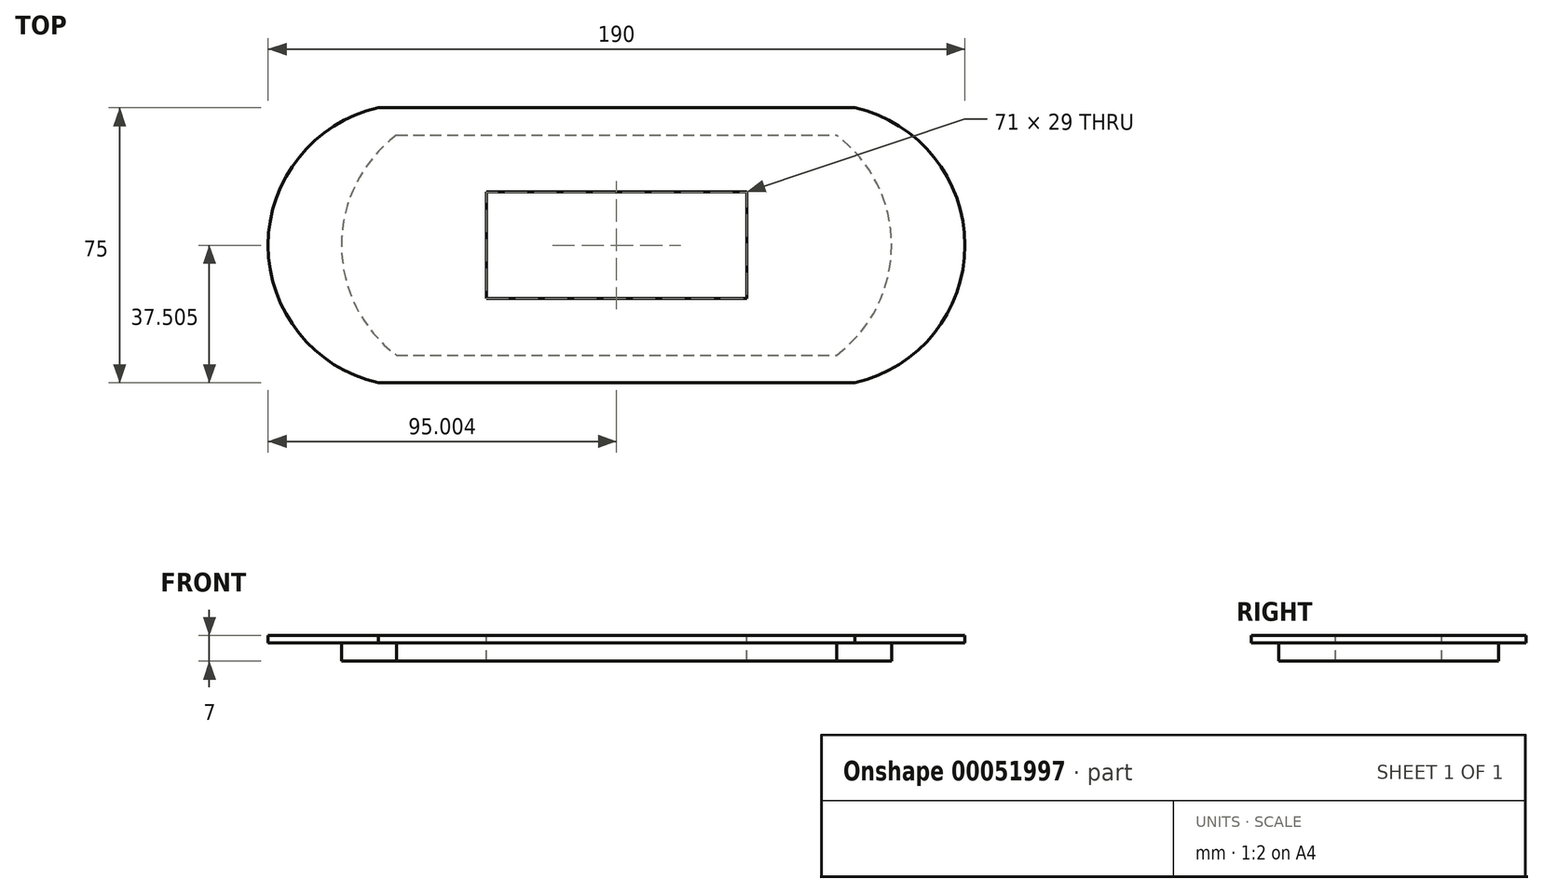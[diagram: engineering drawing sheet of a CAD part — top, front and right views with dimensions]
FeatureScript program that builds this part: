
annotation { "Feature Type Name" : "Feature", "Feature Type Description" : "" }
export const myFeature = defineFeature(function(context is Context, id is Id, definition is map)
    precondition{}
    {
        {
            var Q0;
            Q0=qCreatedBy(makeId("Top.planeOp"),FACE);
            var sketch = newSketch(context, id + "F5", { "sketchPlane" : qUnion([Q0])});
            skLineSegment(sketch, "E0.bottom", {"start": v(43.83, -33.43) * mm, "end": v(233.83, -33.43) * mm, "construction": true});
            skLineSegment(sketch, "E0.top", {"start": v(43.83, 41.57) * mm, "end": v(233.83, 41.57) * mm, "construction": true});
            skLineSegment(sketch, "E0.left", {"start": v(43.83, -33.43) * mm, "end": v(43.83, 41.57) * mm, "construction": true});
            skLineSegment(sketch, "E0.right", {"start": v(233.83, -33.43) * mm, "end": v(233.83, 41.57) * mm, "construction": true});
            skLineSegment(sketch, "E1.bottom", {"start": v(73.83, 41.57) * mm, "end": v(203.83, 41.57) * mm});
            skLineSegment(sketch, "E1.top", {"start": v(73.83, -33.43) * mm, "end": v(203.83, -33.43) * mm});
            skArc(sketch, "E2", {"start": v(73.83, 41.57) * mm, "mid": v(43.83, 4.07) * mm, "end": v(73.83, -33.43) * mm});
            skArc(sketch, "E3", {"start": v(203.83, -33.43) * mm, "mid": v(233.83, 4.07) * mm, "end": v(203.83, 41.57) * mm});
            skSolve(sketch);
        }
        {
            var Q0;
            Q0=makeQuery(id+"F5.imprint","IMPRINT",FACE,{"disambiguationData":[TD([[makeQuery(id+"F5.imprint","IMPRINT",EDGE,{"derivedFrom":sQuery(id+"F5.wireOp",EDGE,"E1.bottom")}),-1.0]])]});
            extrude(context, id + "F0", {"entities" : qUnion([Q0]), "depth" : 2 * mm});
        }
        {
            var Q0;
            Q0=makeQuery(id+"F0.opExtrude","CAP_FACE",FACE,{"disambiguationData":[OSD([sQuery(id+"F5.wireOp",EDGE,"E1.bottom"),sQuery(id+"F5.wireOp",EDGE,"E1.top"),sQuery(id+"F5.wireOp",EDGE,"E2"),sQuery(id+"F5.wireOp",EDGE,"E3")])],"isStart":false});
            var sketch = newSketch(context, id + "F1", { "sketchPlane" : qUnion([Q0])});
            skLineSegment(sketch, "E4.bottom", {"start": v(103.33, 18.57) * mm, "end": v(174.33, 18.57) * mm});
            skLineSegment(sketch, "E4.top", {"start": v(103.33, -10.43) * mm, "end": v(174.33, -10.43) * mm});
            skLineSegment(sketch, "E4.left", {"start": v(103.33, 18.57) * mm, "end": v(103.33, -10.43) * mm});
            skLineSegment(sketch, "E4.right", {"start": v(174.33, 18.57) * mm, "end": v(174.33, -10.43) * mm});
            skLineSegment(sketch, "E5", {"start": v(73.83, 41.57) * mm, "end": v(103.33, 18.57) * mm, "construction": true});
            skLineSegment(sketch, "E6", {"start": v(174.33, -10.43) * mm, "end": v(203.83, -33.43) * mm, "construction": true});
            skLineSegment(sketch, "E7", {"start": v(103.33, -10.43) * mm, "end": v(73.83, -33.43) * mm, "construction": true});
            skLineSegment(sketch, "E8", {"start": v(174.33, 18.57) * mm, "end": v(203.83, 41.57) * mm, "construction": true});
            skSolve(sketch);
        }
        {
            var Q0;
            Q0=makeQuery(id+"F5.imprint","IMPRINT",FACE,{"disambiguationData":[TD([[makeQuery(id+"F5.imprint","IMPRINT",EDGE,{"derivedFrom":sQuery(id+"F5.wireOp",EDGE,"E1.bottom")}),-1.0]])]});
            var sketch = newSketch(context, id + "F2", { "sketchPlane" : qUnion([Q0])});
            skLineSegment(sketch, "E9.bottom", {"start": v(78.83, -25.93) * mm, "end": v(198.83, -25.93) * mm});
            skLineSegment(sketch, "E9.top", {"start": v(78.83, 34.08) * mm, "end": v(198.83, 34.08) * mm});
            skArc(sketch, "E10", {"start": v(78.83, 34.08) * mm, "mid": v(63.83, 4.07) * mm, "end": v(78.83, -25.93) * mm});
            skArc(sketch, "E11", {"start": v(198.83, -25.93) * mm, "mid": v(213.83, 4.07) * mm, "end": v(198.83, 34.08) * mm});
            skLineSegment(sketch, "E12", {"start": v(78.83, -25.93) * mm, "end": v(63.83, -25.93) * mm, "construction": true});
            skLineSegment(sketch, "E13", {"start": v(63.83, -25.93) * mm, "end": v(63.83, 34.08) * mm, "construction": true});
            skLineSegment(sketch, "E14", {"start": v(63.83, 34.08) * mm, "end": v(78.83, 34.08) * mm, "construction": true});
            skLineSegment(sketch, "E15", {"start": v(198.83, -25.93) * mm, "end": v(213.83, -25.93) * mm, "construction": true});
            skLineSegment(sketch, "E16", {"start": v(213.83, -25.93) * mm, "end": v(213.83, 34.08) * mm, "construction": true});
            skLineSegment(sketch, "E17", {"start": v(213.83, 34.08) * mm, "end": v(198.83, 34.08) * mm, "construction": true});
            skLineSegment(sketch, "E18", {"start": v(73.83, -33.43) * mm, "end": v(78.83, -25.93) * mm});
            skLineSegment(sketch, "E19", {"start": v(78.83, 34.08) * mm, "end": v(73.83, 41.57) * mm});
            skLineSegment(sketch, "E20", {"start": v(198.83, 34.08) * mm, "end": v(203.83, 41.57) * mm});
            skLineSegment(sketch, "E21", {"start": v(198.83, -25.93) * mm, "end": v(203.83, -33.43) * mm});
            skSolve(sketch);
        }
        {
            var Q0;
            Q0=makeQuery(id+"F2.imprint","IMPRINT",FACE,{"disambiguationData":[TD([[makeQuery(id+"F2.imprint","IMPRINT",EDGE,{"derivedFrom":sQuery(id+"F2.wireOp",EDGE,"E9.bottom")}),1.0]])]});
            extrude(context, id + "F3", {"entities" : qUnion([Q0]), "operationType" : NewBodyOperationType.ADD, "oppositeDirection" : true, "depth" : 5 * mm});
        }
        {
            var Q0;
            Q0=makeQuery(id+"F1.imprint","IMPRINT",FACE,{"disambiguationData":[TD([[makeQuery(id+"F1.imprint","IMPRINT",EDGE,{"derivedFrom":sQuery(id+"F1.wireOp",EDGE,"E4.bottom")}),-1.0]])]});
            var Q1;
            Q1=makeQuery(id+"F3.opExtrude","CAP_FACE",FACE,{"disambiguationData":[OSD([sQuery(id+"F2.wireOp",EDGE,"E9.bottom"),sQuery(id+"F2.wireOp",EDGE,"E9.top"),sQuery(id+"F2.wireOp",EDGE,"E10"),sQuery(id+"F2.wireOp",EDGE,"E11")])],"isStart":false});
            extrude(context, id + "F4", {"entities" : qUnion([Q0]), "operationType" : NewBodyOperationType.REMOVE, "endBound" : BoundingType.UP_TO_SURFACE, "oppositeDirection" : true, "endBoundEntityFace" : qUnion([Q1]), "depth" : 25 * mm});
        }
    });
